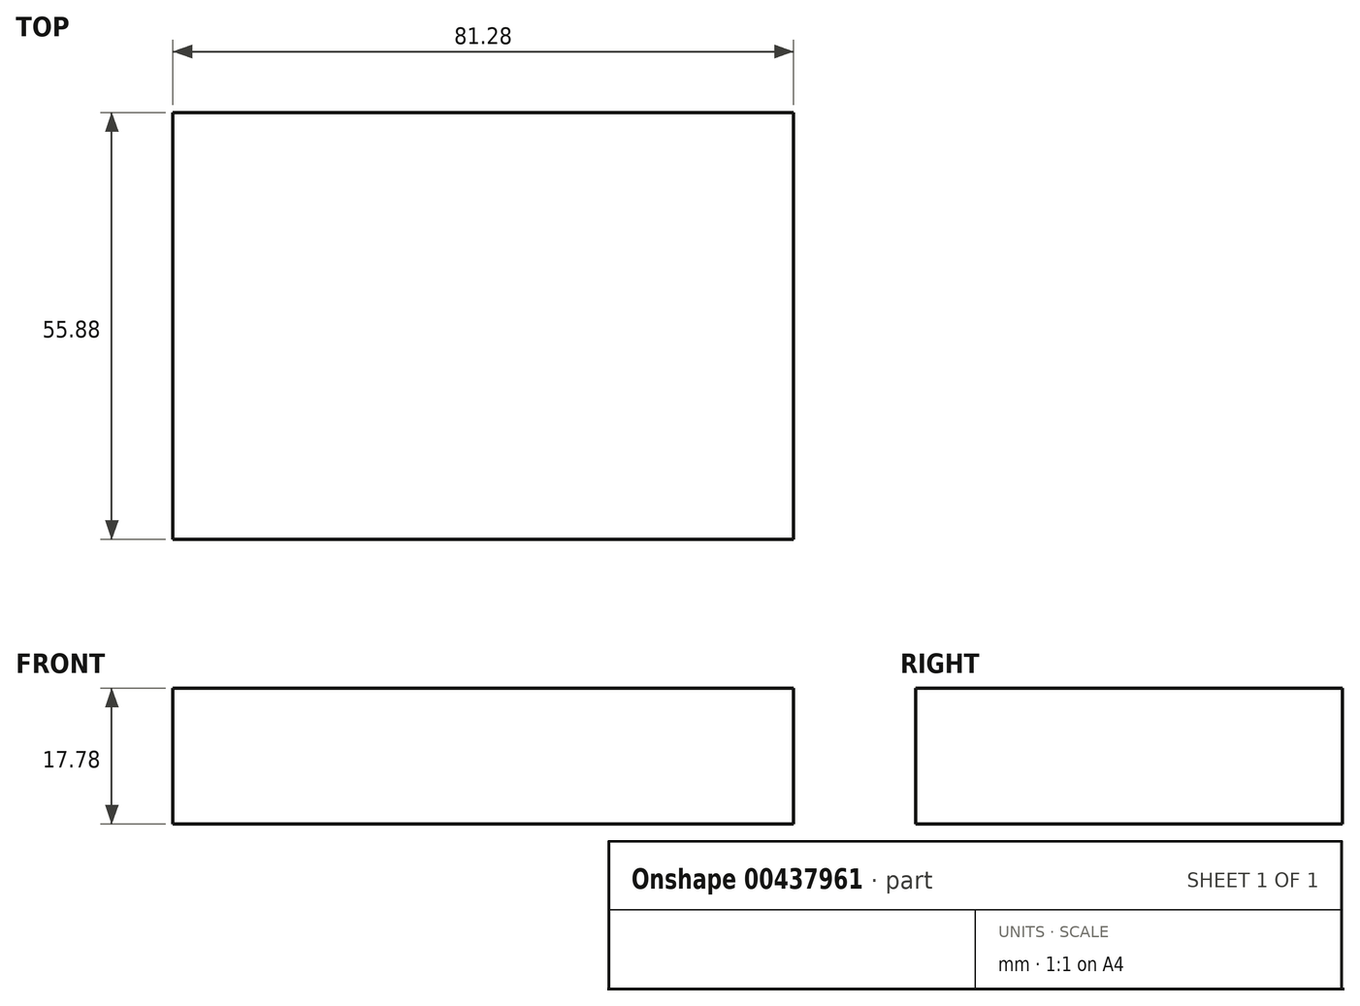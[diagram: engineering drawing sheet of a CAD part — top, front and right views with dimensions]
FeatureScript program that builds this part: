
annotation { "Feature Type Name" : "Feature", "Feature Type Description" : "" }
export const myFeature = defineFeature(function(context is Context, id is Id, definition is map)
    precondition{}
    {
        {
            var Q0;
            Q0=qCreatedBy(makeId("Front.planeOp"),FACE);
            var sketch = newSketch(context, id + "F0", { "sketchPlane" : qUnion([Q0])});
            skLineSegment(sketch, "E0.bottom", {"start": v(-55.97, -1.98) * mm, "end": v(25.3, -1.98) * mm});
            skLineSegment(sketch, "E0.top", {"start": v(-55.97, -19.76) * mm, "end": v(25.3, -19.76) * mm});
            skLineSegment(sketch, "E0.left", {"start": v(-55.97, -1.98) * mm, "end": v(-55.97, -19.76) * mm});
            skLineSegment(sketch, "E0.right", {"start": v(25.3, -1.98) * mm, "end": v(25.3, -19.76) * mm});
            skSolve(sketch);
        }
        {
            var Q0;
            Q0=qSketchRegion(id+"F0",true);
            extrude(context, id + "F1", {"entities" : qUnion([Q0]), "depth" : 55.88 * mm});
        }
    });
